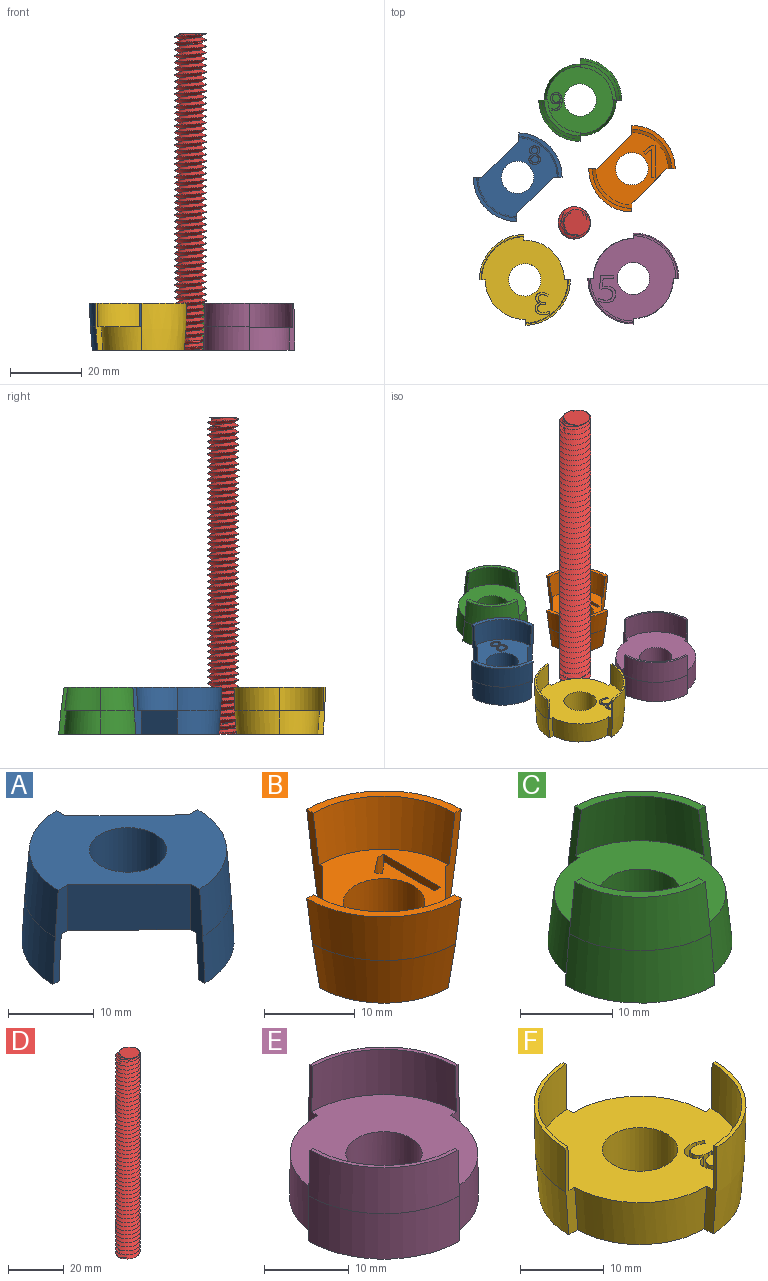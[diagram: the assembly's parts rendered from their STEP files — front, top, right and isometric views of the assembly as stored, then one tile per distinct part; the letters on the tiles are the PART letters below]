
ASSEMBLY  parts=6 mates=5
PART A: 51 faces, bbox 24.8x24.7x13 mm
  f0: plane 23.01x23mm, normal (0,0,1), area 240.8mm2, adj f2,f6,f7,f9,f12,f13,f14,f15
  f1: plane 22x21.99mm, normal (0,0,-1), area 210.4mm2, adj f5,f6,f7,f10,f12,f13,f14,f15
  f2: revolved ~12x11.7mm, area 118.5mm2, adj f0,f3,f6,f7
  f3: revolved ~12.36x12.05mm, area 122.6mm2, adj f2,f4,f6,f7
  f4: plane 12.36x12.06mm, normal (0,0,-1), area 18.3mm2, adj f3,f5,f6,f7
  f5: revolved ~11.36x11.07mm, area 112.5mm2, adj f1,f4,f6,f7
  f6: plane 13x2.36mm, normal (1,0.03,0), area 18mm2, adj f0,f1,f2,f3,f4,f5,f15
  f7: plane 13.03x2.39mm, normal (0,-1,0), area 18mm2, adj f0,f1,f2,f3,f4,f5,f14
  f8: revolved ~12.36x12.05mm, area 122.6mm2, adj f9,f11,f12,f13
  f9: revolved ~12x11.7mm, area 118.5mm2, adj f0,f8,f12,f13
  f10: revolved ~11.36x11.07mm, area 112.5mm2, adj f1,f11,f12,f13
  f11: plane 12.36x12.06mm, normal (0,0,-1), area 18.3mm2, adj f8,f10,f12,f13
  f12: plane 13.03x2.39mm, normal (-1,-0.03,0), area 18mm2, adj f0,f1,f8,f9,f10,f11,f14
  f13: plane 13.03x2.39mm, normal (0,1,0), area 18mm2, adj f0,f1,f8,f9,f10,f11,f15
  f14: plane 10.26x10mm, normal (-0.7,-0.72,0), area 93.1mm2, adj f0,f1,f7,f12
  f15: plane 10.26x10mm, normal (0.7,0.72,0), area 93.1mm2, adj f0,f1,f6,f13
  f16: cylinder r=4.5mm len=9mm, axis (0,0,1), area 183.8mm2, adj f0,f1
  f17: extruded ~5x1.07mm, area 5.7mm2, adj f1,f18,f47,f48
  f18: extruded ~5x1.07mm, area 5.7mm2, adj f1,f17,f19,f48
  f19: extruded ~5x0.87mm, area 5mm2, adj f1,f18,f20,f48
  f20: extruded ~5x0.67mm, area 3.6mm2, adj f1,f19,f21,f48
  f21: extruded ~5x0.73mm, area 4.6mm2, adj f1,f20,f22,f48
  f22: extruded ~5x0.86mm, area 5.3mm2, adj f1,f21,f23,f48
  f23: extruded ~5x0.73mm, area 4mm2, adj f1,f22,f24,f48
  f24: extruded ~5x0.98mm, area 5.6mm2, adj f1,f23,f25,f48
  f25: extruded ~5x1.18mm, area 6.3mm2, adj f1,f24,f26,f48
  f26: extruded ~5x1.22mm, area 6.5mm2, adj f1,f25,f27,f48
  f27: extruded ~5x0.99mm, area 5.6mm2, adj f1,f26,f28,f48
  f28: extruded ~5x1.33mm, area 8.9mm2, adj f1,f27,f29,f48
  f29: extruded ~5x0.67mm, area 4.4mm2, adj f1,f28,f30,f48
  f30: extruded ~5x0.69mm, area 3.6mm2, adj f1,f29,f47,f48
  f31: extruded ~5x0.68mm, area 3.6mm2, adj f32,f45,f48,f50
  f32: extruded ~5x0.67mm, area 3.6mm2, adj f31,f33,f48,f50
  f33: extruded ~5x0.54mm, area 3.1mm2, adj f32,f34,f48,f50
  f34: extruded ~5x0.54mm, area 2.9mm2, adj f33,f35,f48,f50
  f35: extruded ~5x0.74mm, area 4.4mm2, adj f34,f36,f48,f50
  f36: extruded ~5x0.69mm, area 4.1mm2, adj f35,f37,f48,f50
  f37: extruded ~5x0.55mm, area 3mm2, adj f36,f45,f48,f50
  f38: extruded ~5x0.63mm, area 3.4mm2, adj f39,f46,f48,f49
  f39: extruded ~5x0.63mm, area 3.6mm2, adj f38,f40,f48,f49
  f40: extruded ~5x0.8mm, area 4.2mm2, adj f39,f41,f48,f49
  f41: extruded ~5x0.79mm, area 4.2mm2, adj f40,f42,f48,f49
  f42: extruded ~5x0.65mm, area 3.7mm2, adj f41,f43,f48,f49
  f43: extruded ~5x0.59mm, area 3.3mm2, adj f42,f44,f48,f49
  f44: extruded ~5x0.92mm, area 5.3mm2, adj f43,f46,f48,f49
  f45: extruded ~5x0.54mm, area 3.1mm2, adj f31,f37,f48,f50
  f46: extruded ~5x0.73mm, area 4.4mm2, adj f38,f44,f48,f49
  f47: extruded ~5x0.86mm, area 4.9mm2, adj f1,f17,f30,f48
  f48: plane 5.1x3.26mm, normal (0,0,-1), area 7.3mm2, adj f17,f18,f19,f20,f21,f22,f23,f24
  f49: plane 2.15x1.97mm, normal (0,0,-1), area 3.2mm2, adj f38,f39,f40,f41,f42,f43,f44,f46
  f50: plane 1.83x1.73mm, normal (0,0,-1), area 2.4mm2, adj f31,f32,f33,f34,f35,f36,f37,f45
PART B: 34 faces, bbox 24.9x24.9x13.9 mm
  f0: plane 20.2x20.2mm, normal (0,0,1), area 177.9mm2, adj f10,f14,f15,f16,f19,f20,f21,f22
  f1: revolved ~6.24x1.3mm, area 3.9mm2, adj f6,f15,f22
  f2: cylinder r=8.52mm len=1.15mm, axis (0,0,1), area 0.3mm2, adj f5,f9,f19,f22
  f3: cylinder r=8.52mm len=1.15mm, axis (0,0,1), area 0.3mm2, adj f8,f9,f14,f23
  f4: revolved ~6.24x1.3mm, area 3.9mm2, adj f7,f20,f23
  f5: revolved ~6.24x1.3mm, area 3.9mm2, adj f2,f19,f22
  f6: cylinder r=8.52mm len=1.15mm, axis (0,0,1), area 0.3mm2, adj f1,f9,f15,f22
  f7: cylinder r=8.52mm len=1.15mm, axis (0,0,1), area 0.3mm2, adj f4,f9,f20,f23
  f8: revolved ~6.24x1.3mm, area 3.9mm2, adj f3,f14,f23
  f9: plane 20x20mm, normal (0,0,-1), area 183.1mm2, adj f2,f3,f6,f7,f13,f14,f15,f17
  f10: revolved ~11x11mm, area 109.1mm2, adj f0,f11,f14,f15
  f11: plane 12.01x12.01mm, normal (0,0,1), area 18.2mm2, adj f10,f12,f14,f15
  f12: revolved ~12.01x12.01mm, area 119.5mm2, adj f11,f13,f14,f15
  f13: revolved ~11.12x11.12mm, area 109.4mm2, adj f9,f12,f14,f15
  f14: plane 13x3.5mm, normal (1,0,0), area 16.4mm2, adj f0,f3,f8,f9,f10,f11,f12,f13
  f15: plane 13.1x3.6mm, normal (0,1,0), area 16.4mm2, adj f0,f1,f6,f9,f10,f11,f12,f13
  f16: revolved ~11x11mm, area 109.1mm2, adj f0,f18,f19,f20
  f17: revolved ~13x12.01mm, area 228.9mm2, adj f9,f18,f19,f20
  f18: plane 12.01x12.01mm, normal (0,0,1), area 18.2mm2, adj f16,f17,f19,f20
  f19: plane 13.86x4.35mm, normal (-1,0,0), area 16.5mm2, adj f0,f2,f5,f9,f16,f17,f18
  f20: plane 13.86x4.35mm, normal (0,-1,0), area 16.5mm2, adj f0,f4,f7,f9,f16,f17,f18
  f21: cylinder r=4.5mm len=9mm, axis (0,0,1), area 183.8mm2, adj f0,f9
  f22: plane 9.95x9.95mm, normal (-0.71,0.71,0), area 77.6mm2, adj f0,f1,f2,f5,f6,f9
  f23: plane 9.95x9.95mm, normal (0.71,-0.71,0), area 77.6mm2, adj f0,f3,f4,f7,f8,f9
  f24: plane 5x0.99mm, normal (0,1,0), area 4.9mm2, adj f0,f25,f32,f33
  f25: plane 8.9x5mm, normal (-1,0,0), area 44.5mm2, adj f0,f24,f26,f33
  f26: plane 5x0.85mm, normal (0,-1,0), area 4.3mm2, adj f0,f25,f27,f33
  f27: plane 5x2.35mm, normal (0.61,-0.79,0), area 14.9mm2, adj f0,f26,f28,f33
  f28: plane 5x0.69mm, normal (0.79,0.61,0), area 4.4mm2, adj f0,f27,f29,f33
  f29: extruded ~5x1.45mm, area 9.4mm2, adj f0,f28,f30,f33
  f30: extruded ~5x0.29mm, area 2mm2, adj f0,f29,f31,f33
  f31: extruded ~5x1.5mm, area 7.5mm2, adj f0,f30,f32,f33
  f32: plane 6.34x5mm, normal (1,0,0), area 31.7mm2, adj f0,f24,f31,f33
  f33: plane 8.9x3.21mm, normal (0,0,1), area 10.8mm2, adj f24,f25,f26,f27,f28,f29,f30,f31
PART C: 45 faces, bbox 23.1x23.1x13.1 mm
  f0: plane 19.69x19.69mm, normal (0,0,1), area 215.6mm2, adj f1,f2,f4,f8,f9,f10,f14,f15
  f1: revolved ~10x10mm, area 99.4mm2, adj f0,f3,f9,f14
  f2: revolved ~10x10mm, area 99.4mm2, adj f0,f3,f8,f15
  f3: plane 23.01x23.01mm, normal (0,0,-1), area 301.4mm2, adj f1,f2,f7,f8,f9,f11,f14,f15
  f4: revolved ~9.85x9.85mm, area 97.2mm2, adj f0,f5,f8,f9
  f5: plane 10x10mm, normal (0,0,1), area 15.1mm2, adj f4,f6,f8,f9
  f6: revolved ~10.85x10.85mm, area 107.6mm2, adj f5,f7,f8,f9
  f7: revolved ~11.51x11.51mm, area 114.9mm2, adj f3,f6,f8,f9
  f8: plane 13.01x2.52mm, normal (1,0,0), area 16.4mm2, adj f0,f2,f3,f4,f5,f6,f7
  f9: plane 13.14x2.65mm, normal (0,1,0), area 16.4mm2, adj f0,f1,f3,f4,f5,f6,f7
  f10: revolved ~9.85x9.85mm, area 97.2mm2, adj f0,f13,f14,f15
  f11: revolved ~11.51x11.51mm, area 114.9mm2, adj f3,f12,f14,f15
  f12: revolved ~10.85x10.85mm, area 107.6mm2, adj f11,f13,f14,f15
  f13: plane 10x10mm, normal (0,0,1), area 15.1mm2, adj f10,f12,f14,f15
  f14: plane 13.01x2.52mm, normal (-1,0,0), area 16.4mm2, adj f0,f1,f3,f10,f11,f12,f13
  f15: plane 13.14x2.65mm, normal (0,-1,0), area 16.4mm2, adj f0,f2,f3,f10,f11,f12,f13
  f16: cylinder r=4.5mm len=9mm, axis (0,0,1), area 183.8mm2, adj f0,f3
  f17: extruded ~5x0.75mm, area 4.2mm2, adj f18,f42,f43,f44
  f18: extruded ~5x0.57mm, area 3mm2, adj f17,f19,f43,f44
  f19: extruded ~5x0.47mm, area 3.1mm2, adj f18,f20,f43,f44
  f20: extruded ~5x0.66mm, area 3.4mm2, adj f19,f21,f43,f44
  f21: extruded ~5x0.45mm, area 2.4mm2, adj f20,f22,f43,f44
  f22: extruded ~5x0.41mm, area 2.7mm2, adj f21,f23,f43,f44
  f23: extruded ~5x0.57mm, area 2.9mm2, adj f22,f24,f43,f44
  f24: extruded ~5x0.74mm, area 4.1mm2, adj f23,f25,f43,f44
  f25: extruded ~5x0.77mm, area 4.1mm2, adj f24,f42,f43,f44
  f26: extruded ~5x2.91mm, area 21mm2, adj f0,f27,f41,f43
  f27: extruded ~5x1.17mm, area 6mm2, adj f0,f26,f28,f43
  f28: extruded ~5x0.76mm, area 4.8mm2, adj f0,f27,f29,f43
  f29: extruded ~5x0.88mm, area 4.7mm2, adj f0,f28,f30,f43
  f30: extruded ~5x1.14mm, area 6.3mm2, adj f0,f29,f31,f43
  f31: extruded ~5x1.22mm, area 6.6mm2, adj f0,f30,f32,f43
  f32: extruded ~5x1.1mm, area 6mm2, adj f0,f31,f33,f43
  f33: extruded ~5x1.04mm, area 5.7mm2, adj f0,f32,f34,f43
  f34: extruded ~5x0.7mm, area 3.6mm2, adj f0,f33,f35,f43
  f35: extruded ~5x0.5mm, area 3.3mm2, adj f0,f34,f36,f43
  f36: plane 5x0.04mm, normal (0,1,0), area 0.2mm2, adj f0,f35,f37,f43
  f37: extruded ~5x1.54mm, area 8.2mm2, adj f0,f36,f38,f43
  f38: extruded ~5x1.23mm, area 6.9mm2, adj f0,f37,f39,f43
  f39: extruded ~5x0.62mm, area 3.1mm2, adj f0,f38,f40,f43
  f40: plane 5x0.49mm, normal (1,0,0), area 2.4mm2, adj f0,f39,f41,f43
  f41: extruded ~5x0.62mm, area 3.1mm2, adj f0,f26,f40,f43
  f42: extruded ~5x0.87mm, area 4.6mm2, adj f17,f25,f43,f44
  f43: plane 5.1x3.24mm, normal (0,0,1), area 6.4mm2, adj f17,f18,f19,f20,f21,f22,f23,f24
  f44: plane 2.23x2.11mm, normal (0,0,1), area 3.8mm2, adj f17,f18,f19,f20,f21,f22,f23,f24
PART D: 4 faces, bbox 10.1x11.4x91.2 mm
  f0: plane 8.62x8.6mm, normal (0,0,1), area 42.6mm2, adj f1,f2
  f1: bspline ~89.94x10.22mm, area 2025.3mm2, adj f0,f2,f3
  f2: bspline ~89.94x10.22mm, area 2025.3mm2, adj f0,f1,f3
  f3: plane 8.6x8.59mm, normal (0,0,-1), area 42.6mm2, adj f1,f2
PART E: 36 faces, bbox 25.4x25.4x13.1 mm
  f0: plane 24.18x24.18mm, normal (0,0,1), area 346.3mm2, adj f1,f2,f4,f8,f9,f10,f13,f14
  f1: revolved ~11.15x11.15mm, area 110.2mm2, adj f0,f3,f9,f13
  f2: revolved ~11.15x11.15mm, area 110.2mm2, adj f0,f3,f8,f14
  f3: plane 25.3x25.3mm, normal (0,0,-1), area 383mm2, adj f1,f2,f7,f8,f9,f12,f13,f14
  f4: revolved ~12.09x12.09mm, area 126.2mm2, adj f0,f5,f8,f9
  f5: plane 12.36x12.36mm, normal (0,0,1), area 9.5mm2, adj f4,f6,f8,f9
  f6: revolved ~12.58x12.58mm, area 127.5mm2, adj f5,f7,f8,f9
  f7: revolved ~12.65x12.65mm, area 129mm2, adj f3,f6,f8,f9
  f8: plane 13.09x1.66mm, normal (1,0,0), area 12.8mm2, adj f0,f2,f3,f4,f5,f6,f7
  f9: plane 13.1x1.66mm, normal (0,1,0), area 12.8mm2, adj f0,f1,f3,f4,f5,f6,f7
  f10: revolved ~12.09x12.09mm, area 126.2mm2, adj f0,f11,f13,f14
  f11: plane 12.36x12.36mm, normal (0,0,1), area 9.5mm2, adj f10,f12,f13,f14
  f12: revolved ~13x12.65mm, area 256.5mm2, adj f3,f11,f13,f14
  f13: plane 13.01x1.58mm, normal (-1,0,0), area 12.8mm2, adj f0,f1,f3,f10,f11,f12
  f14: plane 13.09x1.67mm, normal (0,-1,0), area 12.8mm2, adj f0,f2,f3,f10,f11,f12
  f15: cylinder r=4.5mm len=9mm, axis (0,0,1), area 178.1mm2, adj f0,f3
  f16: extruded ~5x1.84mm, area 9.8mm2, adj f0,f17,f34,f35
  f17: extruded ~5x1.16mm, area 5.8mm2, adj f0,f16,f18,f35
  f18: plane 5x2.22mm, normal (-1,0.08,0), area 11.1mm2, adj f0,f17,f19,f35
  f19: plane 5x2.96mm, normal (0,1,0), area 14.8mm2, adj f0,f18,f20,f35
  f20: plane 5x0.77mm, normal (-1,0,0), area 3.9mm2, adj f0,f19,f21,f35
  f21: plane 5x3.67mm, normal (0,-1,0), area 18.4mm2, adj f0,f20,f22,f35
  f22: plane 5x3.46mm, normal (1,-0.08,0), area 17.3mm2, adj f0,f21,f23,f35
  f23: plane 5x0.44mm, normal (0.54,0.84,0), area 2.6mm2, adj f0,f22,f24,f35
  f24: extruded ~5x1.28mm, area 6.5mm2, adj f0,f23,f25,f35
  f25: extruded ~5x1.89mm, area 14mm2, adj f0,f24,f26,f35
  f26: extruded ~5x1.21mm, area 6.8mm2, adj f0,f25,f27,f35
  f27: extruded ~5x1.38mm, area 7.4mm2, adj f0,f26,f28,f35
  f28: extruded ~5x1.04mm, area 5.2mm2, adj f0,f27,f29,f35
  f29: extruded ~5x0.88mm, area 4.8mm2, adj f0,f28,f30,f35
  f30: plane 5x0.81mm, normal (1,0,0), area 4mm2, adj f0,f29,f31,f35
  f31: extruded ~5x1.9mm, area 9.8mm2, adj f0,f30,f32,f35
  f32: extruded ~5x2.01mm, area 10.8mm2, adj f0,f31,f33,f35
  f33: extruded ~5x1.8mm, area 10mm2, adj f0,f32,f34,f35
  f34: extruded ~5x1.58mm, area 8.9mm2, adj f0,f16,f33,f35
  f35: plane 7.49x4.65mm, normal (0,0,1), area 12.7mm2, adj f16,f17,f18,f19,f20,f21,f22,f23
PART F: 45 faces, bbox 25.6x25.6x13.3 mm
  f0: revolved ~11.29x11mm, area 112mm2, adj f2,f3,f8,f14
  f1: revolved ~11.29x11mm, area 112mm2, adj f2,f3,f9,f13
  f2: plane 24x23.99mm, normal (0,0,1), area 343.8mm2, adj f0,f1,f4,f8,f9,f12,f13,f14
  f3: plane 24.02x24.01mm, normal (0,0,-1), area 335.3mm2, adj f0,f1,f7,f8,f9,f10,f13,f14
  f4: revolved ~12.15x11.84mm, area 121.9mm2, adj f2,f5,f8,f9
  f5: plane 12.65x12.33mm, normal (0,0,1), area 9.6mm2, adj f4,f6,f8,f9
  f6: revolved ~12.65x12.32mm, area 126.5mm2, adj f5,f7,f8,f9
  f7: revolved ~12.5x12.19mm, area 123.8mm2, adj f3,f6,f8,f9
  f8: plane 13x2.15mm, normal (1,0.03,0), area 13mm2, adj f0,f2,f3,f4,f5,f6,f7
  f9: plane 13.3x2.45mm, normal (0,-1,0), area 13mm2, adj f1,f2,f3,f4,f5,f6,f7
  f10: revolved ~13x12.65mm, area 250.3mm2, adj f3,f11,f13,f14
  f11: plane 12.65x12.33mm, normal (0,0,1), area 9.6mm2, adj f10,f12,f13,f14
  f12: revolved ~12.15x11.84mm, area 121.9mm2, adj f2,f11,f13,f14
  f13: plane 13.3x2.45mm, normal (-1,-0.03,0), area 13mm2, adj f1,f2,f3,f10,f11,f12
  f14: plane 13.3x2.45mm, normal (0,1,0), area 13mm2, adj f0,f2,f3,f10,f11,f12
  f15: cylinder r=4.5mm len=9mm, axis (0,0,1), area 183.2mm2, adj f2,f3
  f16: extruded ~5x1.09mm, area 6.2mm2, adj f2,f17,f43,f44
  f17: extruded ~5x0.93mm, area 5mm2, adj f2,f16,f18,f44
  f18: extruded ~5x0.91mm, area 5.2mm2, adj f2,f17,f19,f44
  f19: plane 5x0.03mm, normal (1,0,0), area 0.2mm2, adj f2,f18,f20,f44
  f20: extruded ~5x1.06mm, area 5.9mm2, adj f2,f19,f21,f44
  f21: extruded ~5x0.96mm, area 5.2mm2, adj f2,f20,f22,f44
  f22: extruded ~5x1.31mm, area 7.5mm2, adj f2,f21,f23,f44
  f23: extruded ~5x1.68mm, area 8.8mm2, adj f2,f22,f24,f44
  f24: extruded ~5x0.87mm, area 4.3mm2, adj f2,f23,f25,f44
  f25: extruded ~5x0.76mm, area 4mm2, adj f2,f24,f26,f44
  f26: plane 5x0.64mm, normal (-1,0,0), area 3.2mm2, adj f2,f25,f27,f44
  f27: extruded ~5x0.82mm, area 4.4mm2, adj f2,f26,f28,f44
  f28: extruded ~5x0.83mm, area 4.2mm2, adj f2,f27,f29,f44
  f29: extruded ~5x1.54mm, area 11.2mm2, adj f2,f28,f30,f44
  f30: extruded ~5x1.7mm, area 11.4mm2, adj f2,f29,f31,f44
  f31: plane 5x0.59mm, normal (0,1,0), area 2.9mm2, adj f2,f30,f32,f44
  f32: plane 5x0.58mm, normal (-1,0,0), area 2.9mm2, adj f2,f31,f33,f44
  f33: plane 5x0.59mm, normal (0,-1,0), area 3mm2, adj f2,f32,f34,f44
  f34: extruded ~5x1.1mm, area 5.8mm2, adj f2,f33,f35,f44
  f35: extruded ~5x0.85mm, area 4.9mm2, adj f2,f34,f36,f44
  f36: extruded ~5x0.68mm, area 3.9mm2, adj f2,f35,f37,f44
  f37: extruded ~5x0.81mm, area 4.3mm2, adj f2,f36,f38,f44
  f38: extruded ~5x0.74mm, area 3.7mm2, adj f2,f37,f39,f44
  f39: extruded ~5x0.79mm, area 4.4mm2, adj f2,f38,f40,f44
  f40: plane 5x0.46mm, normal (-0.8,0.6,0), area 2.8mm2, adj f2,f39,f41,f44
  f41: extruded ~5x0.84mm, area 4.8mm2, adj f2,f40,f42,f44
  f42: extruded ~5x1.01mm, area 5.1mm2, adj f2,f41,f43,f44
  f43: extruded ~5x1.35mm, area 7.2mm2, adj f2,f16,f42,f44
  f44: plane 6.12x3.89mm, normal (0,0,1), area 8.2mm2, adj f16,f17,f18,f19,f20,f21,f22,f23
PLACE A rot(axis=(0,1,0),180deg) t=(-44.01,-3.32,54.51)mm
PLACE B t=(-12.22,-0.95,2.51)mm fixed
PLACE C t=(-26.6,18.18,-49.49)mm
PLACE D t=(-178.33,81.32,-1.49)mm
PLACE E t=(-11.83,-31.45,-23.49)mm
PLACE F t=(-42.01,-31.83,-10.49)mm
MATE planar B.f2 <-> C.f16  axis (0,0,-1) through (-12.22,-0.95,2.51)mm
MATE planar B.f2 <-> A.f16  axis (0,0,-1) through (-12.22,-0.95,2.51)mm
MATE planar B.f2 <-> F.f15  axis (0,0,-1) through (-12.22,-0.95,2.51)mm
MATE planar D.f3 <-> B.f2  axis (0,0,-1) through (-28.19,-18.93,2.51)mm
MATE planar B.f2 <-> E.f15  axis (0,0,-1) through (-12.22,-0.95,2.51)mm
